# Revit family: CENTUM T-Lock M12x40
name_source: partatom
category: HLS-Bauteile
units: mm (PartAtom-declared; Revit-internal decimal feet)

## family parameters
Arbeitsebenenbasiert = Ja
Beim Laden mit Abzugskörper schneiden = Nein
Bemaßung runder Anschluss = Durchmesser verwenden
Beschriftungsausrichtung beibehalten = Nein
Gemeinsam genutzt = Ja
Immer vertikal = Nein
Raumberechnungspunkt = Nein
Teiletyp = Normal

## types (1)
- CENTUM T-Lock M12x40
    Abmessung = M12 x 40 mm
    Artikelnummer = 1610011000
    B = 23 mm
    Baulänge = 34 mm
    Breite Hammerkopf = 12.5 mm
    D = 13 mm
    D0 = 13 mm
    Durchmesser U-Scheibe = 23.5 mm
    EAN = 4250928436658
    Fabrikat = MEFA
    Festigkeitsklasse = 10.9
    Firma = MEFA Befestigungs- und Montagesysteme GmbH
    Gewicht = 0.12 kg
    Gewicht pro Bauteil = 0.12 kg
    Gewinde = M12
    Kurztext1 = CENTUM T-Lock
    Kurztext2 = M12 x 40 mm
    L = 24 mm  [stored 0.0787402 ft]
    L1 = 34 mm
    Länge Gewinde = 40 mm  [stored 0.131234 ft]
    Länge Hammerkopf = 28 mm
    Material = Stahl
    Mengeneinheit = St
    Oberflaeche = Zink-Nickel
    Profil = CENTUM
    Profiltyp = XL 80, XL 100, XL 120, XL 200
    S = 10 mm  [stored 0.0328084 ft]
    Stärke Hammerkopf = 12 mm
    Stärke Scheibe = 10 mm
    Vorgabe-Ansicht = 1219 mm
    d1 = 11 mm
    vpe = 50

note: [stored X ft] marks values corroborated as IEEE doubles in the binary element streams (Revit-internal decimal feet)

## geometry (parser evidence)
native form markers: Sweep x2
no freeform markers — native parametric forms only
